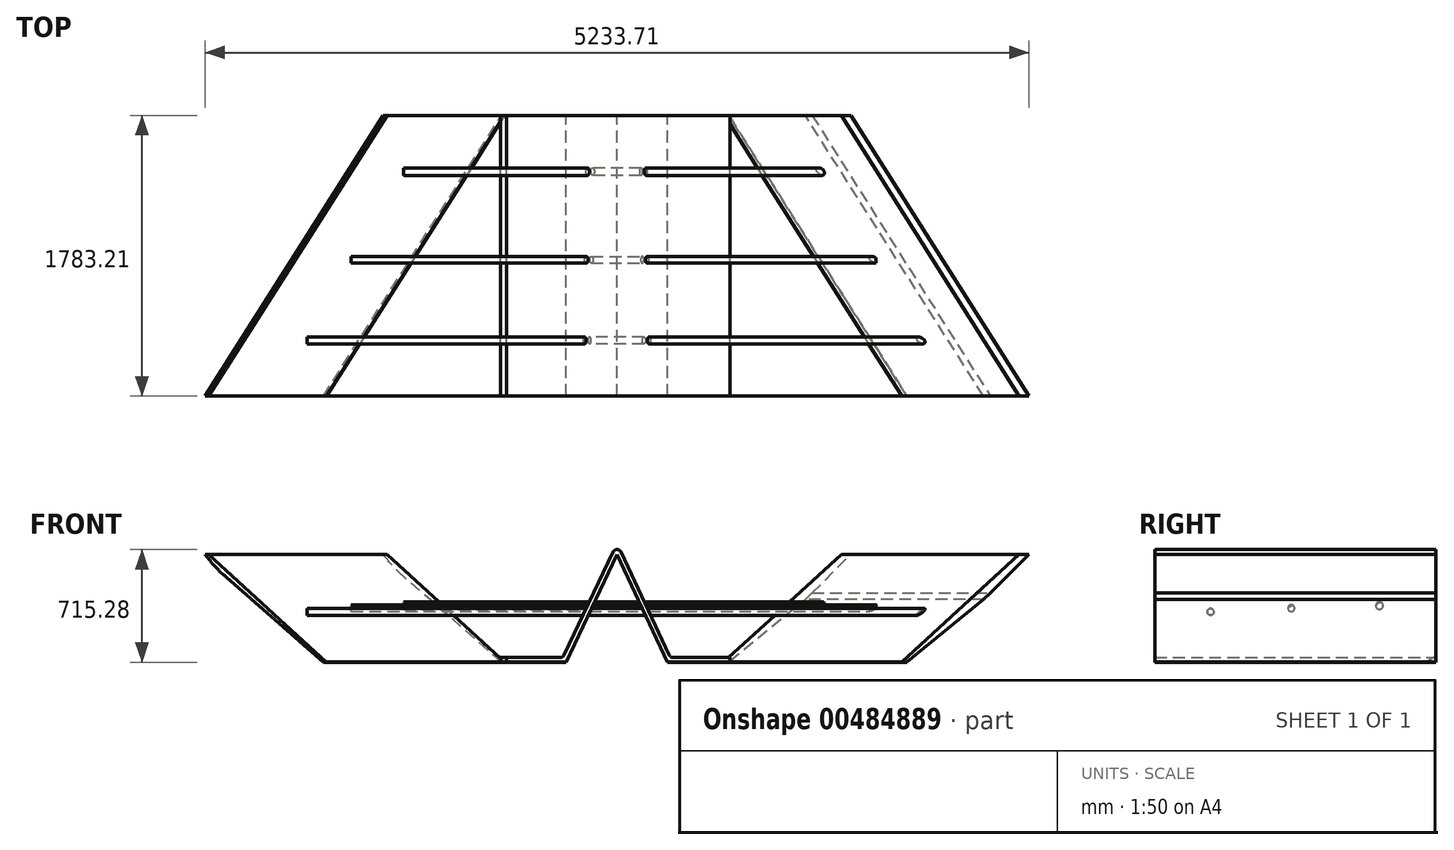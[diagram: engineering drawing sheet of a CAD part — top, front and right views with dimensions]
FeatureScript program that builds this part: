
annotation { "Feature Type Name" : "Feature", "Feature Type Description" : "" }
export const myFeature = defineFeature(function(context is Context, id is Id, definition is map)
    precondition{}
    {
        {
            var Q0;
            Q0=qCreatedBy(makeId("Top.planeOp"),FACE);
            var sketch = newSketch(context, id + "F0", { "sketchPlane" : qUnion([Q0])});
            skLineSegment(sketch, "E0", {"start": v(-77.7, 1429.67) * mm, "end": v(-1209.66, -353.44) * mm});
            skLineSegment(sketch, "E1", {"start": v(-1209.66, -353.44) * mm, "end": v(-1981.26, -353.44) * mm});
            skLineSegment(sketch, "E2", {"start": v(-1981.26, -353.44) * mm, "end": v(-849.3, 1429.67) * mm});
            skLineSegment(sketch, "E3", {"start": v(-849.3, 1429.67) * mm, "end": v(-77.7, 1429.67) * mm});
            skLineSegment(sketch, "E4", {"start": v(635.6, 1429.67) * mm, "end": v(635.6, -353.44) * mm});
            skLineSegment(sketch, "E5.MirrorCS", {"start": v(3252.45, -353.44) * mm, "end": v(2120.5, 1429.67) * mm});
            skLineSegment(sketch, "E6.MirrorCS", {"start": v(2480.85, -353.44) * mm, "end": v(3252.45, -353.44) * mm});
            skLineSegment(sketch, "E7.MirrorCS", {"start": v(2120.5, 1429.67) * mm, "end": v(1348.9, 1429.67) * mm});
            skLineSegment(sketch, "E8.0", {"start": v(1324.1, 1413.84) * mm, "end": v(2452.94, -371.09) * mm});
            skLineSegment(sketch, "E9", {"start": v(2480.85, -353.44) * mm, "end": v(2421.9, -353.44) * mm});
            skLineSegment(sketch, "E10", {"start": v(1348.9, 1429.67) * mm, "end": v(1270.63, 1429.67) * mm});
            skLineSegment(sketch, "E11", {"start": v(1324.1, 1413.84) * mm, "end": v(1314.09, 1429.67) * mm});
            skSolve(sketch);
        }
        {
            var Q0;
            Q0 = qSketchRegion(id + "F0", true);
            extrude(context, id + "F1", {"entities" : qUnion([Q0]), "depth" : 685.8 * mm});
        }
        {
            var Q0;
            Q0=qCreatedBy(makeId("Top.planeOp"),FACE);
            var sketch = newSketch(context, id + "F2", { "sketchPlane" : qUnion([Q0])});
            skLineSegment(sketch, "E12", {"start": v(-77.7, 1429.5) * mm, "end": v(1344.75, 1429.5) * mm});
            skLineSegment(sketch, "E13", {"start": v(633.53, 1429.5) * mm, "end": v(633.53, -804.37) * mm});
            skLineSegment(sketch, "E14", {"start": v(-77.7, 1429.5) * mm, "end": v(-1209.66, -353.44) * mm});
            skLineSegment(sketch, "E15", {"start": v(-1209.66, -353.44) * mm, "end": v(310.68, -353.44) * mm});
            skLineSegment(sketch, "E16", {"start": v(310.68, -353.44) * mm, "end": v(310.68, 1429.5) * mm});
            skLineSegment(sketch, "E17.MirrorCS", {"start": v(956.38, -353.44) * mm, "end": v(956.38, 1429.5) * mm});
            skLineSegment(sketch, "E18.MirrorCS", {"start": v(2476.71, -353.44) * mm, "end": v(956.38, -353.44) * mm});
            skLineSegment(sketch, "E19.MirrorCS", {"start": v(1344.75, 1429.5) * mm, "end": v(2476.71, -353.44) * mm});
            skSolve(sketch);
        }
        {
            var Q0;
            Q0 = qSketchRegion(id + "F2", true);
            extrude(context, id + "F3", {"entities" : qUnion([Q0]), "depth" : 2.54 * mm});
        }
        {
            var Q0;
            Q0=qCreatedBy(makeId("Front.planeOp"),FACE);
            var sketch = newSketch(context, id + "F4", { "sketchPlane" : qUnion([Q0])});
            skLineSegment(sketch, "E20.0", {"start": v(1352, 685.8) * mm, "end": v(1352, 0) * mm});
            skLineSegment(sketch, "E21.0", {"start": v(-64.56, 685.8) * mm, "end": v(-64.56, 0) * mm});
            skLineSegment(sketch, "E22", {"start": v(1352, 685.8) * mm, "end": v(-80.82, 685.8) * mm});
            skLineSegment(sketch, "E23", {"start": v(635.6, 685.8) * mm, "end": v(635.6, 0) * mm});
            skLineSegment(sketch, "E24.0", {"start": v(-77.7, 0) * mm, "end": v(310.68, 0) * mm});
            skLineSegment(sketch, "E25.0", {"start": v(956.38, 0) * mm, "end": v(1344.75, 0) * mm});
            skLineSegment(sketch, "E26", {"start": v(310.68, 0) * mm, "end": v(635.6, 685.8) * mm});
            skLineSegment(sketch, "E27", {"start": v(956.38, 0) * mm, "end": v(635.6, 685.8) * mm});
            skLineSegment(sketch, "E28.0", {"start": v(974.7, 28.78) * mm, "end": v(628.36, 769.2) * mm});
            skLineSegment(sketch, "E28.1", {"start": v(974.7, 28.78) * mm, "end": v(1390.53, 28.78) * mm});
            skLineSegment(sketch, "E29.0", {"start": v(292.46, 28.78) * mm, "end": v(639.47, 761.2) * mm});
            skLineSegment(sketch, "E29.1", {"start": v(-99.37, 28.78) * mm, "end": v(292.46, 28.78) * mm});
            skLineSegment(sketch, "E30", {"start": v(1352, 0) * mm, "end": v(1352, 28.78) * mm});
            skLineSegment(sketch, "E31", {"start": v(1352, 0) * mm, "end": v(956.38, 0) * mm});
            skSolve(sketch);
        }
        {
            var Q0;
            {var subQ0=sQuery(id+"F4.wireOp",EDGE,"E22");var subQ1=makeQuery(id+"F4.imprint","INTERSECT",VERTEX,{"derivedFrom":[subQ0,sQuery(id+"F4.wireOp",EDGE,"E26")]});Q0=makeQuery(id+"F4.imprint","IMPRINT",FACE,{"disambiguationData":[TD([[makeQuery(id+"F4.imprint","IMPRINT",EDGE,{"disambiguationData":[TD([[subQ1,1.0]])],"derivedFrom":subQ0}),-1.0]])]});}
            var Q1;
            {var subQ3=sQuery(id+"F4.wireOp",EDGE,"E26");Q1=makeQuery(id+"F4.imprint","IMPRINT",FACE,{"disambiguationData":[TD([[makeQuery(id+"F4.imprint","IMPRINT",EDGE,{"derivedFrom":subQ3}),1.0]])]});}
            var Q2;
            {var subQ6=sQuery(id+"F4.wireOp",EDGE,"E27");Q2=makeQuery(id+"F4.imprint","IMPRINT",FACE,{"disambiguationData":[TD([[makeQuery(id+"F4.imprint","IMPRINT",EDGE,{"derivedFrom":subQ6}),-1.0]])]});}
            extrude(context, id + "F5", {"entities" : qUnion([Q0, Q1, Q2]), "operationType" : NewBodyOperationType.ADD, "depth" : 353.06 * mm});
        }
        {
            var Q0;
            {var subQ0=sQuery(id+"F4.wireOp",EDGE,"E26");Q0=makeQuery(id+"F4.imprint","IMPRINT",FACE,{"disambiguationData":[TD([[makeQuery(id+"F4.imprint","IMPRINT",EDGE,{"derivedFrom":subQ0}),1.0]])]});}
            var Q1;
            {var subQ2=sQuery(id+"F4.wireOp",EDGE,"E28.0");var subQ4=sQuery(id+"F4.wireOp",EDGE,"E29.0");var subQ5=makeQuery(id+"F4.imprint","INTERSECT",VERTEX,{"derivedFrom":[subQ2,subQ4]});Q1=makeQuery(id+"F4.imprint","IMPRINT",FACE,{"disambiguationData":[TD([[makeQuery(id+"F4.imprint","IMPRINT",EDGE,{"disambiguationData":[TD([[subQ5,1.0]])],"derivedFrom":subQ2}),1.0]])]});}
            var Q2;
            {var subQ6=sQuery(id+"F4.wireOp",EDGE,"E27");Q2=makeQuery(id+"F4.imprint","IMPRINT",FACE,{"disambiguationData":[TD([[makeQuery(id+"F4.imprint","IMPRINT",EDGE,{"derivedFrom":subQ6}),-1.0]])]});}
            extrude(context, id + "F6", {"entities" : qUnion([Q0, Q1, Q2]), "oppositeDirection" : true, "depth" : 1429.77 * mm});
        }
        {
            var Q0;
            Q0=makeQuery(id+"F6.opExtrude","SWEPT_EDGE",EDGE,{"disambiguationData":[OSD([sQuery(id+"F4.wireOp",EDGE,"E28.0"),sQuery(id+"F4.wireOp",EDGE,"E29.0")])]});
            var Q1;
            Q1=makeQuery(id+"F5.opExtrude","SWEPT_EDGE",EDGE,{"disambiguationData":[OSD([sQuery(id+"F4.wireOp",EDGE,"E28.0"),sQuery(id+"F4.wireOp",EDGE,"E29.0")])]});
            var Q2;
            Q2=makeQuery(id+"F5.opExtrude","SWEPT_EDGE",EDGE,{"disambiguationData":[OSD([sQuery(id+"F4.wireOp",EDGE,"E28.0"),sQuery(id+"F4.wireOp",EDGE,"E28.1")])]});
            var Q3;
            Q3=makeQuery(id+"F6.opExtrude","SWEPT_EDGE",EDGE,{"disambiguationData":[OSD([sQuery(id+"F4.wireOp",EDGE,"E28.0"),sQuery(id+"F4.wireOp",EDGE,"E28.1")])]});
            var Q4;
            Q4=makeQuery(id+"F5.opExtrude","SWEPT_EDGE",EDGE,{"disambiguationData":[OSD([sQuery(id+"F4.wireOp",EDGE,"E29.0"),sQuery(id+"F4.wireOp",EDGE,"E29.1")])]});
            var Q5;
            Q5=makeQuery(id+"F6.opExtrude","SWEPT_EDGE",EDGE,{"disambiguationData":[OSD([sQuery(id+"F4.wireOp",EDGE,"E29.0"),sQuery(id+"F4.wireOp",EDGE,"E29.1")])]});
            fillet(context, id + "F7", {"entities" : qUnion([Q0, Q1, Q2, Q3, Q4, Q5]), "radius" : 28.27 * mm, "tangentPropagation" : true, "allowEdgeOverflow" : false});
        }
        {
            var Q0;
            Q0=makeQuery(id+"F1.opExtrude","CAP_EDGE",EDGE,{"disambiguationData":[OSD([sQuery(id+"F0.wireOp",EDGE,"E2")])],"isStart":true});
            var Q1;
            Q1=makeQuery(id+"F1.opExtrude","CAP_EDGE",EDGE,{"disambiguationData":[OSD([sQuery(id+"F0.wireOp",EDGE,"E5.MirrorCS")])],"isStart":true});
            chamfer(context, id + "F8", {"entities" : qUnion([Q0, Q1]), "chamferType" : ChamferType.OFFSET_ANGLE, "width" : 635 * mm, "oppositeDirection" : false, "angle" : 46 * degree, "tangentPropagation" : true});
        }
        {
            var Q0;
            {var subQ0=sQuery(id+"F0.wireOp",EDGE,"E2");Q0=makeQuery(id+"F8.opChamfer","BLEND_EDGE",EDGE,{"blendedFrom":[makeQuery(id+"F1.opExtrude","CAP_EDGE",EDGE,{"disambiguationData":[OSD([subQ0])],"isStart":true}),makeQuery(id+"F1.opExtrude","SWEPT_FACE",FACE,{"disambiguationData":[OSD([subQ0])]})],"blendedInto":[makeQuery(id+"F1.opExtrude","SWEPT_FACE",FACE,{"disambiguationData":[OSD([subQ0])]})]});}
            fillet(context, id + "F9", {"entities" : qUnion([Q0]), "radius" : 898.7 * mm, "tangentPropagation" : true, "allowEdgeOverflow" : false});
        }
        {
            var Q0;
            Q0=makeQuery(id+"F1.opExtrude","CAP_EDGE",EDGE,{"disambiguationData":[OSD([sQuery(id+"F0.wireOp",EDGE,"E0")])],"isStart":false});
            var Q1;
            Q1=makeQuery(id+"F1.opExtrude","CAP_EDGE",EDGE,{"disambiguationData":[OSD([sQuery(id+"F0.wireOp",EDGE,"E8.0"),sQuery(id+"F0.wireOp",EDGE,"E11")])],"isStart":false});
            chamfer(context, id + "F10", {"entities" : qUnion([Q0, Q1]), "chamferType" : ChamferType.OFFSET_ANGLE, "width" : 685.8 * mm, "oppositeDirection" : false, "angle" : 42.6 * degree, "tangentPropagation" : true});
        }
        {
            var Q0;
            {var subQ0=sQuery(id+"F0.wireOp",EDGE,"E5.MirrorCS");Q0=makeQuery(id+"F8.opChamfer","BLEND_EDGE",EDGE,{"blendedFrom":[makeQuery(id+"F1.opExtrude","CAP_EDGE",EDGE,{"disambiguationData":[OSD([subQ0])],"isStart":true}),makeQuery(id+"F1.opExtrude","SWEPT_FACE",FACE,{"disambiguationData":[OSD([subQ0])]})],"blendedInto":[makeQuery(id+"F1.opExtrude","SWEPT_FACE",FACE,{"disambiguationData":[OSD([subQ0])]})]});}
            chamfer(context, id + "F11", {"entities" : qUnion([Q0]), "chamferType" : ChamferType.OFFSET_ANGLE, "width" : 50.8 * mm, "oppositeDirection" : false, "angle" : 40 * degree, "tangentPropagation" : true});
        }
        {
            var Q0;
            {var subQ0=sQuery(id+"F0.wireOp",EDGE,"E5.MirrorCS");Q0=makeQuery(id+"F11.opChamfer","BLEND_EDGE",EDGE,{"blendedFrom":[makeQuery(id+"F8.opChamfer","BLEND_EDGE",EDGE,{"blendedFrom":[makeQuery(id+"F1.opExtrude","CAP_EDGE",EDGE,{"disambiguationData":[OSD([subQ0])],"isStart":true}),makeQuery(id+"F1.opExtrude","SWEPT_FACE",FACE,{"disambiguationData":[OSD([subQ0])]})],"blendedInto":[makeQuery(id+"F1.opExtrude","SWEPT_FACE",FACE,{"disambiguationData":[OSD([subQ0])]})]}),makeQuery(id+"F8.opChamfer","BLEND_FACE",FACE,{"disambiguationData":[OSD([subQ0])]})],"blendedInto":[makeQuery(id+"F8.opChamfer","BLEND_FACE",FACE,{"disambiguationData":[OSD([subQ0])]})]});}
            chamfer(context, id + "F12", {"entities" : qUnion([Q0]), "width" : 508 * mm, "tangentPropagation" : true});
        }
        {
            var Q0;
            Q0=qCreatedBy(makeId("Right.planeOp"),FACE);
            var sketch = newSketch(context, id + "F13", { "sketchPlane" : qUnion([Q0])});
            skCircle(sketch, "E32", {"center": v(0, 319.54) * mm, "radius": 21.28 * mm});
            skCircle(sketch, "E33", {"center": v(512.63, 342.52) * mm, "radius": 21.5 * mm});
            skCircle(sketch, "E34", {"center": v(1072.47, 359.23) * mm, "radius": 23.63 * mm});
            skSolve(sketch);
        }
        {
            var Q0;
            Q0 = qSketchRegion(id + "F13", true);
            extrude(context, id + "F14", {"entities" : qUnion([Q0]), "depth" : 1958.34 * mm});
        }
        {
            var Q0;
            Q0=makeQuery(id+"F14.opExtrude","CAP_EDGE",EDGE,{"disambiguationData":[OSD([sQuery(id+"F13.wireOp",EDGE,"E34")])],"isStart":false});
            fillet(context, id + "F15", {"entities" : qUnion([Q0]), "radius" : 19.18 * mm, "tangentPropagation" : true, "allowEdgeOverflow" : false});
        }
        {
            var Q0;
            Q0=makeQuery(id+"F14.opExtrude","CAP_FACE",FACE,{"disambiguationData":[OSD([sQuery(id+"F13.wireOp",EDGE,"E33")])],"isStart":false});
            var Q1;
            Q1=makeQuery(id+"F14.opExtrude","CAP_FACE",FACE,{"disambiguationData":[OSD([sQuery(id+"F13.wireOp",EDGE,"E32")])],"isStart":false});
            extrude(context, id + "F16", {"entities" : qUnion([Q0, Q1]), "depth" : 322.58 * mm});
        }
        {
            var Q0;
            Q0=makeQuery(id+"F16.opExtrude","CAP_FACE",FACE,{"disambiguationData":[OSD([sQuery(id+"F13.wireOp",EDGE,"E32")])],"isStart":false});
            extrude(context, id + "F17", {"entities" : qUnion([Q0]), "depth" : 312.42 * mm});
        }
        {
            var Q0;
            Q0=makeQuery(id+"F14.opExtrude","CAP_FACE",FACE,{"disambiguationData":[OSD([sQuery(id+"F13.wireOp",EDGE,"E34")])],"isStart":true});
            var Q1;
            Q1=makeQuery(id+"F14.opExtrude","CAP_FACE",FACE,{"disambiguationData":[OSD([sQuery(id+"F13.wireOp",EDGE,"E33")])],"isStart":true});
            var Q2;
            Q2=makeQuery(id+"F14.opExtrude","CAP_FACE",FACE,{"disambiguationData":[OSD([sQuery(id+"F13.wireOp",EDGE,"E32")])],"isStart":true});
            extrude(context, id + "F18", {"entities" : qUnion([Q0, Q1, Q2]), "depth" : 718.82 * mm});
        }
        {
            var Q0;
            Q0=makeQuery(id+"F18.opExtrude","CAP_FACE",FACE,{"disambiguationData":[OSD([sQuery(id+"F13.wireOp",EDGE,"E32")])],"isStart":false});
            var Q1;
            Q1=makeQuery(id+"F18.opExtrude","CAP_FACE",FACE,{"disambiguationData":[OSD([sQuery(id+"F13.wireOp",EDGE,"E33")])],"isStart":false});
            extrude(context, id + "F19", {"entities" : qUnion([Q0, Q1]), "depth" : 332.74 * mm});
        }
        {
            var Q0;
            Q0=makeQuery(id+"F19.opExtrude","CAP_FACE",FACE,{"disambiguationData":[OSD([sQuery(id+"F13.wireOp",EDGE,"E32")])],"isStart":false});
            extrude(context, id + "F20", {"entities" : qUnion([Q0]), "depth" : 281.94 * mm});
        }
        {
            var Q0;
            Q0=makeQuery(id+"F10.opChamfer","BLEND_FACE",FACE,{"disambiguationData":[OSD([sQuery(id+"F0.wireOp",EDGE,"E0")])]});
            var Q1;
            Q1=makeQuery(id+"F3.opExtrude","SWEPT_FACE",FACE,{"disambiguationData":[OSD([sQuery(id+"F2.wireOp",EDGE,"E14")])]});
            var Q2;
            Q2=makeQuery(id+"F10.opChamfer","BLEND_FACE",FACE,{"disambiguationData":[OSD([sQuery(id+"F0.wireOp",EDGE,"E0")])]});
            var Q3;
            Q3=makeQuery(id+"F3.opExtrude","SWEPT_FACE",FACE,{"disambiguationData":[OSD([sQuery(id+"F2.wireOp",EDGE,"E14")])]});
            loft(context, id + "F21", {"bodyType" : ToolBodyType.SURFACE, "sheetProfilesArray" : [{ "sheetProfileEntities" : qUnion([Q0]) }, { "sheetProfileEntities" : qUnion([Q1]) }], "wireProfilesArray" : [{ "wireProfileEntities" : qUnion([Q2]) }, { "wireProfileEntities" : qUnion([Q3]) }]});
        }
        {
            var Q0;
            Q0=makeQuery(id+"F19.opExtrude","SWEPT_BODY",BODY,{"disambiguationData":[OSD([sQuery(id+"F13.wireOp",EDGE,"E33")])]});
            var Q1;
            Q1=makeQuery(id+"F19.opExtrude","SWEPT_BODY",BODY,{"disambiguationData":[OSD([sQuery(id+"F13.wireOp",EDGE,"E32")])]});
            var Q2;
            Q2=makeQuery(id+"F14.opExtrude","SWEPT_BODY",BODY,{"disambiguationData":[OSD([sQuery(id+"F13.wireOp",EDGE,"E32")])]});
            var Q3;
            Q3=makeQuery(id+"F18.opExtrude","SWEPT_BODY",BODY,{"disambiguationData":[OSD([sQuery(id+"F13.wireOp",EDGE,"E32")])]});
            var Q4;
            Q4=makeQuery(id+"F18.opExtrude","SWEPT_BODY",BODY,{"disambiguationData":[OSD([sQuery(id+"F13.wireOp",EDGE,"E34")])]});
            var Q5;
            Q5=makeQuery(id+"F1.opExtrude","SWEPT_BODY",BODY,{"disambiguationData":[OSD([sQuery(id+"F0.wireOp",EDGE,"E5.MirrorCS"),sQuery(id+"F0.wireOp",EDGE,"E6.MirrorCS"),sQuery(id+"F0.wireOp",EDGE,"E7.MirrorCS"),sQuery(id+"F0.wireOp",EDGE,"E8.0"),sQuery(id+"F0.wireOp",EDGE,"E9"),sQuery(id+"F0.wireOp",EDGE,"E10"),sQuery(id+"F0.wireOp",EDGE,"E11")])]});
            var Q6;
            Q6=makeQuery(id+"F3.opExtrude","SWEPT_BODY",BODY,{"disambiguationData":[OSD([sQuery(id+"F2.wireOp",EDGE,"E12"),sQuery(id+"F2.wireOp",EDGE,"E17.MirrorCS"),sQuery(id+"F2.wireOp",EDGE,"E18.MirrorCS"),sQuery(id+"F2.wireOp",EDGE,"E19.MirrorCS")])]});
            var Q7;
            Q7=makeQuery(id+"F20.opExtrude","SWEPT_BODY",BODY,{"disambiguationData":[OSD([sQuery(id+"F13.wireOp",EDGE,"E32")])]});
            var Q8;
            Q8=makeQuery(id+"F6.opExtrude","SWEPT_BODY",BODY,{"disambiguationData":[OSD([sQuery(id+"F4.wireOp",EDGE,"E21.0"),sQuery(id+"F4.wireOp",EDGE,"E24.0"),sQuery(id+"F4.wireOp",EDGE,"E26"),sQuery(id+"F4.wireOp",EDGE,"E27"),sQuery(id+"F4.wireOp",EDGE,"E28.0"),sQuery(id+"F4.wireOp",EDGE,"E28.1"),sQuery(id+"F4.wireOp",EDGE,"E29.0"),sQuery(id+"F4.wireOp",EDGE,"E29.1"),sQuery(id+"F4.wireOp",EDGE,"E30"),sQuery(id+"F4.wireOp",EDGE,"E31")])]});
            var Q9;
            Q9=makeQuery(id+"F3.opExtrude","SWEPT_BODY",BODY,{"disambiguationData":[OSD([sQuery(id+"F2.wireOp",EDGE,"E12"),sQuery(id+"F2.wireOp",EDGE,"E14"),sQuery(id+"F2.wireOp",EDGE,"E15"),sQuery(id+"F2.wireOp",EDGE,"E16")])]});
            var Q10;
            Q10=makeQuery(id+"F18.opExtrude","SWEPT_BODY",BODY,{"disambiguationData":[OSD([sQuery(id+"F13.wireOp",EDGE,"E33")])]});
            var Q11;
            Q11=makeQuery(id+"F16.opExtrude","SWEPT_BODY",BODY,{"disambiguationData":[OSD([sQuery(id+"F13.wireOp",EDGE,"E33")])]});
            var Q12;
            Q12=makeQuery(id+"F14.opExtrude","SWEPT_BODY",BODY,{"disambiguationData":[OSD([sQuery(id+"F13.wireOp",EDGE,"E34")])]});
            var Q13;
            Q13=makeQuery(id+"F14.opExtrude","SWEPT_BODY",BODY,{"disambiguationData":[OSD([sQuery(id+"F13.wireOp",EDGE,"E33")])]});
            var Q14;
            Q14=makeQuery(id+"F16.opExtrude","SWEPT_BODY",BODY,{"disambiguationData":[OSD([sQuery(id+"F13.wireOp",EDGE,"E32")])]});
            var Q15;
            Q15=makeQuery(id+"F17.opExtrude","SWEPT_BODY",BODY,{"disambiguationData":[OSD([sQuery(id+"F13.wireOp",EDGE,"E32")])]});
            booleanBodies(context, id + "F22", {"operationType" : BooleanOperationType.UNION, "tools" : qUnion([Q0, Q1, Q2, Q3, Q4, Q5, Q6, Q7, Q8, Q9, Q10, Q11, Q12, Q13, Q14, Q15])});
        }
        {
            var Q0;
            {var subQ0=sQuery(id+"F4.wireOp",EDGE,"E21.0");Q0=makeQuery(id+"F22.opBoolean","MERGE",FACE,{"derivedFrom":[makeQuery(id+"F5.opExtrude","SWEPT_FACE",FACE,{"disambiguationData":[OSD([subQ0])]}),makeQuery(id+"F6.opExtrude","SWEPT_FACE",FACE,{"disambiguationData":[OSD([subQ0])]})]});}
            extrude(context, id + "F23", {"entities" : qUnion([Q0]), "depth" : 38.1 * mm});
        }
    });
